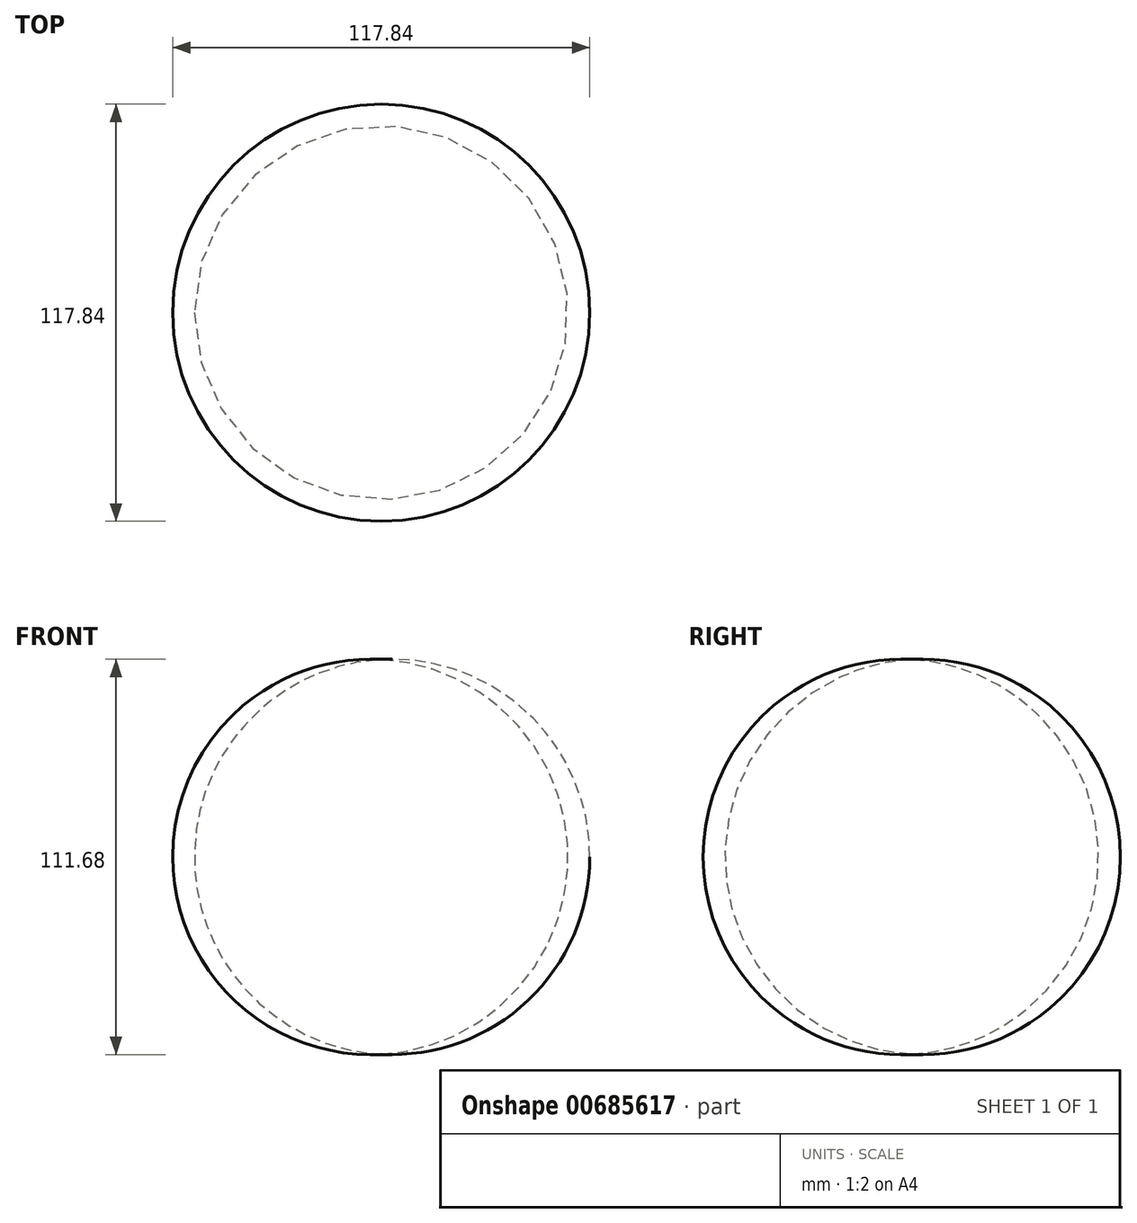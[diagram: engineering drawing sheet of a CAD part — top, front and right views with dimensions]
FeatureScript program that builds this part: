
annotation { "Feature Type Name" : "Feature", "Feature Type Description" : "" }
export const myFeature = defineFeature(function(context is Context, id is Id, definition is map)
    precondition{}
    {
        {
            var Q0;
            Q0=qCreatedBy(makeId("Front.planeOp"),FACE);
            var sketch = newSketch(context, id + "F0", { "sketchPlane" : qUnion([Q0])});
            skArc(sketch, "E0", {"start": v(0, -55.65) * mm, "mid": v(58.92, 0.1) * mm, "end": v(0, 55.85) * mm});
            skLineSegment(sketch, "E1", {"start": v(0, 55.85) * mm, "end": v(0, -55.65) * mm});
            skSolve(sketch);
        }
        {
            var Q0;
            Q0 = qSketchRegion(id + "F0", true);
            var Q1;
            Q1=sQuery(id+"F0.wireOp",EDGE,"E1");
            revolve(context, id + "F1", {"surfaceOperationType" : NewSurfaceOperationType.NEW, "entities" : qUnion([Q0]), "axis" : qUnion([Q1]), "revolveType" : RevolveType.FULL});
        }
    });
